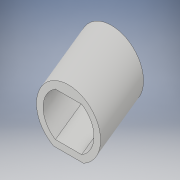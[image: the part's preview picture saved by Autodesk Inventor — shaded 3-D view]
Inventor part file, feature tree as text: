
AUTODESK INVENTOR PART (.ipt)
format: ipt  version: 2017 (Build 210142000, 142)  size: 119,296 bytes
history: native  units: in
note: dims shown in document units (in); Inventor stores cm internally (conversion verified against a paired STEP export)
features: sketch x3, plane x1, sweep x1
ambient origin geometry x8: Origin, YZ Plane, XZ Plane, XY Plane, X Axis, Y Axis, Z Axis, Center Point
bodies: Solid1 (feature_tree)
feature tree (5):
  sketch  "Sketch1"  dims[d0=6.6667in d1=4.0in d2=1.0in d28=8.0in]
  plane  "Work Plane2"
  sweep  "ramp"
  sketch  "Sketch7"  dims[d30=0.0in d31=0.0in]
  sketch  "Sketch6"  dims[d29=0.3779in]
